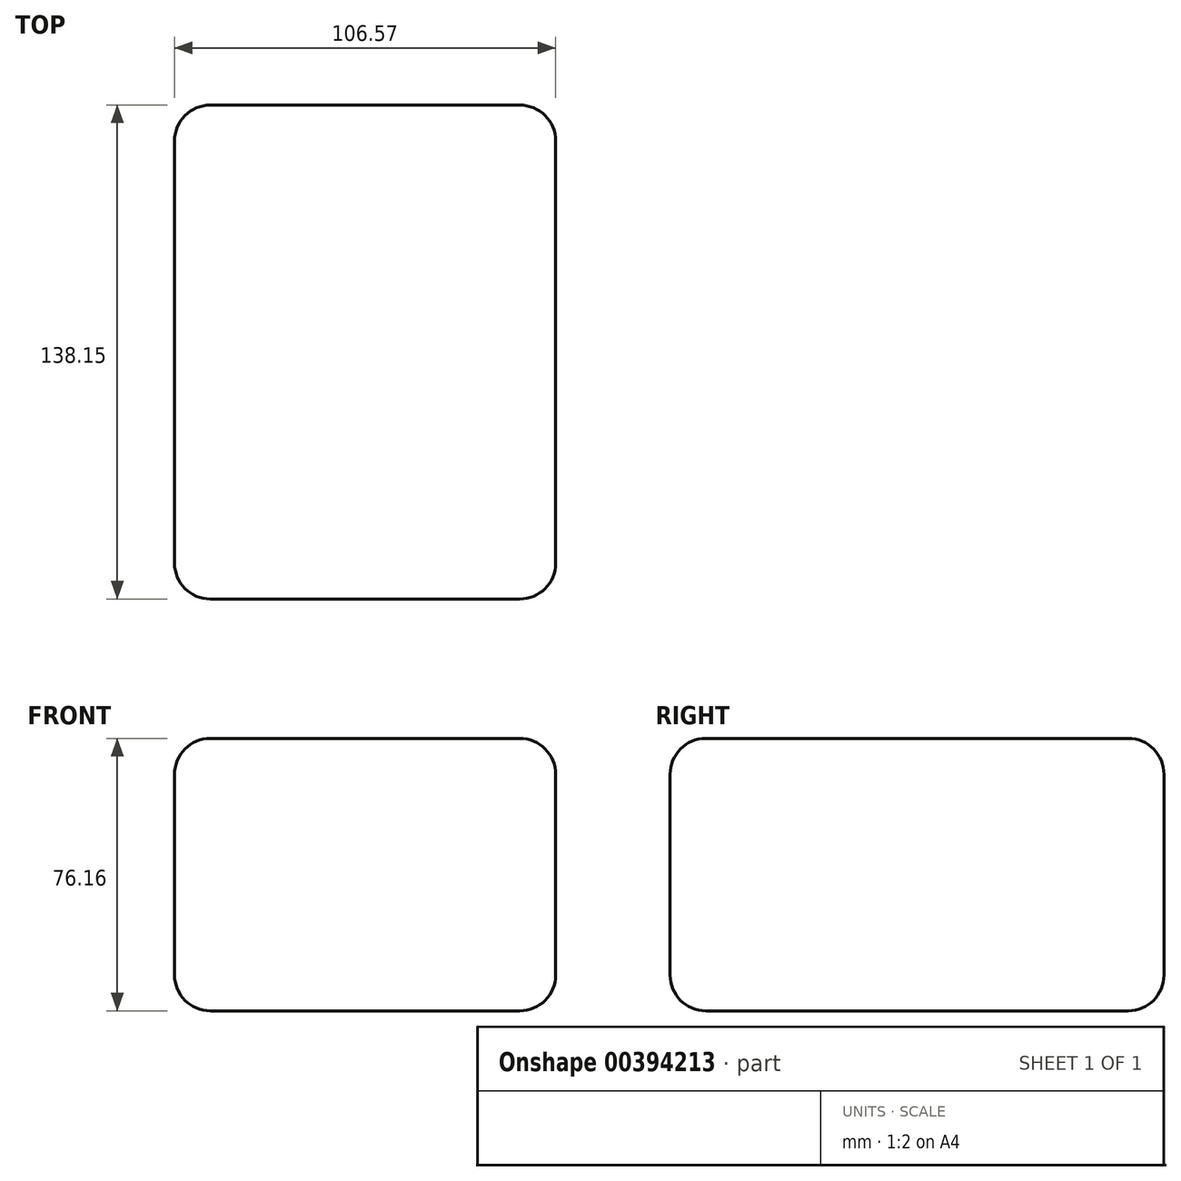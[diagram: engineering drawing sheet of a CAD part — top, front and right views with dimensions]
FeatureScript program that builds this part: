
annotation { "Feature Type Name" : "Feature", "Feature Type Description" : "" }
export const myFeature = defineFeature(function(context is Context, id is Id, definition is map)
    precondition{}
    {
        {
            var Q0;
            Q0=qCreatedBy(makeId("Front.planeOp"),FACE);
            var sketch = newSketch(context, id + "F0", { "sketchPlane" : qUnion([Q0])});
            skLineSegment(sketch, "E0.bottom", {"start": v(7.78, 0) * mm, "end": v(114.35, 0) * mm});
            skLineSegment(sketch, "E0.top", {"start": v(7.78, 76.16) * mm, "end": v(114.35, 76.16) * mm});
            skLineSegment(sketch, "E0.left", {"start": v(7.78, 0) * mm, "end": v(7.78, 76.16) * mm});
            skLineSegment(sketch, "E0.right", {"start": v(114.35, 0) * mm, "end": v(114.35, 76.16) * mm});
            skSolve(sketch);
        }
        {
            var Q0;
            Q0 = qSketchRegion(id + "F0", true);
            extrude(context, id + "F1", {"entities" : qUnion([Q0]), "depth" : 138.15 * mm, "offsetDistance" : 25 * mm});
        }
        {
            var Q0;
            Q0=makeQuery(id+"F1.opExtrude","SWEPT_EDGE",EDGE,{"disambiguationData":[OSD([sQuery(id+"F0.wireOp",EDGE,"E0.top"),sQuery(id+"F0.wireOp",EDGE,"E0.right")])]});
            var Q1;
            Q1=makeQuery(id+"F1.opExtrude","SWEPT_EDGE",EDGE,{"disambiguationData":[OSD([sQuery(id+"F0.wireOp",EDGE,"E0.bottom"),sQuery(id+"F0.wireOp",EDGE,"E0.right")])]});
            var Q2;
            Q2=makeQuery(id+"F1.opExtrude","SWEPT_EDGE",EDGE,{"disambiguationData":[OSD([sQuery(id+"F0.wireOp",EDGE,"E0.top"),sQuery(id+"F0.wireOp",EDGE,"E0.left")])]});
            var Q3;
            Q3=makeQuery(id+"F1.opExtrude","CAP_FACE",FACE,{"disambiguationData":[OSD([sQuery(id+"F0.wireOp",EDGE,"E0.bottom"),sQuery(id+"F0.wireOp",EDGE,"E0.top"),sQuery(id+"F0.wireOp",EDGE,"E0.left"),sQuery(id+"F0.wireOp",EDGE,"E0.right")])],"isStart":false});
            var Q4;
            Q4=makeQuery(id+"F1.opExtrude","CAP_FACE",FACE,{"disambiguationData":[OSD([sQuery(id+"F0.wireOp",EDGE,"E0.bottom"),sQuery(id+"F0.wireOp",EDGE,"E0.top"),sQuery(id+"F0.wireOp",EDGE,"E0.left"),sQuery(id+"F0.wireOp",EDGE,"E0.right")])],"isStart":true});
            var Q5;
            Q5=makeQuery(id+"F1.opExtrude","SWEPT_EDGE",EDGE,{"disambiguationData":[OSD([sQuery(id+"F0.wireOp",EDGE,"E0.bottom"),sQuery(id+"F0.wireOp",EDGE,"E0.left")])]});
            fillet(context, id + "F2", {"entities" : qUnion([Q0, Q1, Q2, Q3, Q4, Q5]), "tangentPropagation" : true, "radius" : 10 * mm, "defaultsChanged" : false, "vertexSettings" : [], "allowEdgeOverflow" : false});
        }
    });
